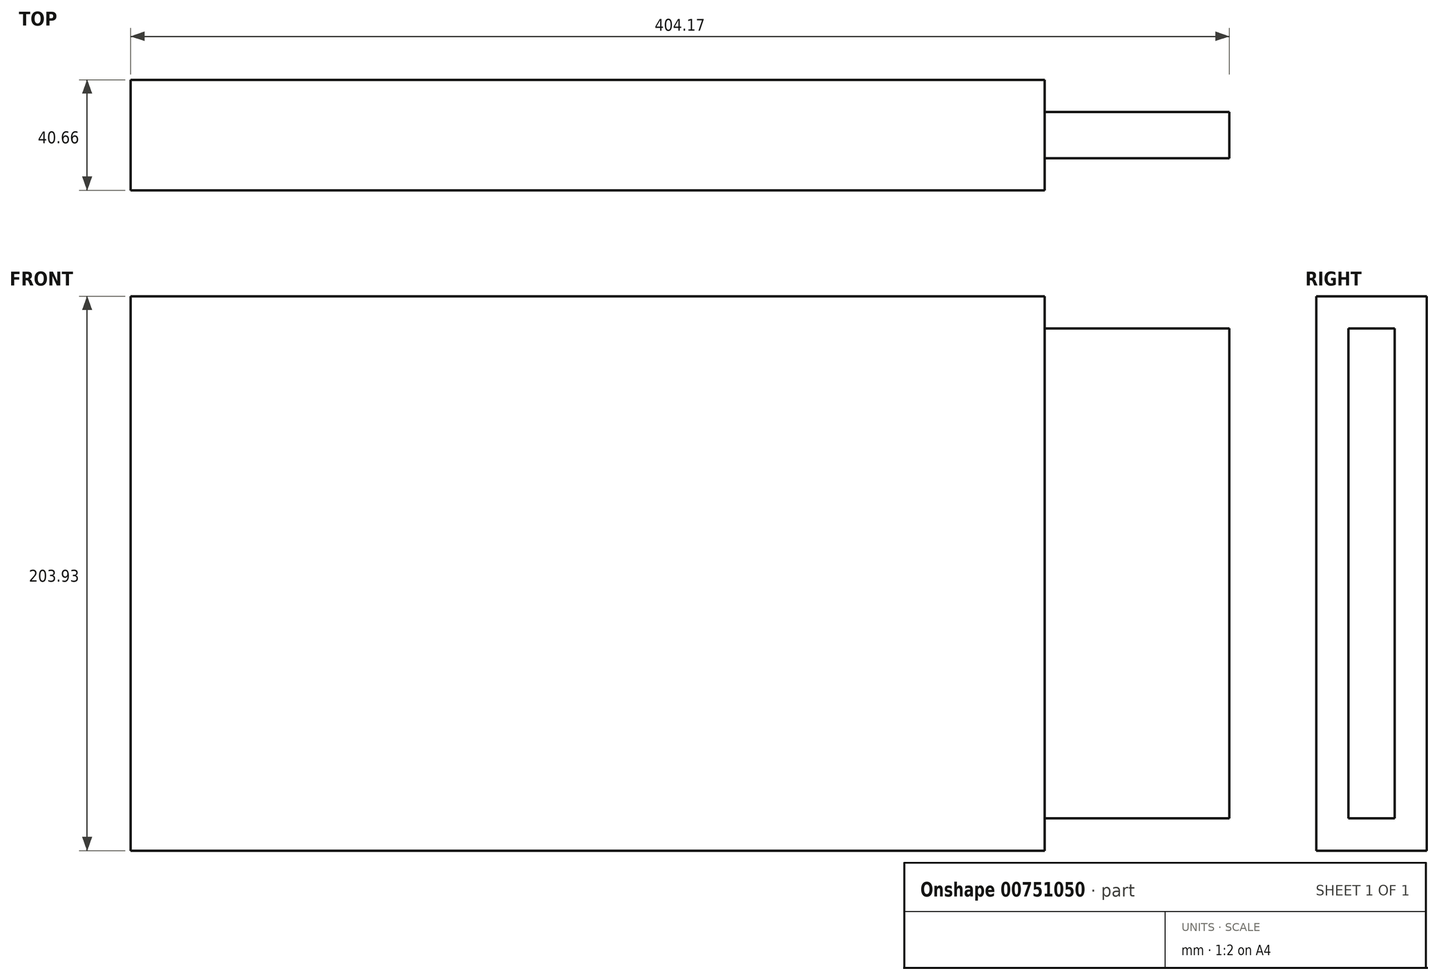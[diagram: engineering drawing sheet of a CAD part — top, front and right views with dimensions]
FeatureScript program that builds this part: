
annotation { "Feature Type Name" : "Feature", "Feature Type Description" : "" }
export const myFeature = defineFeature(function(context is Context, id is Id, definition is map)
    precondition{}
    {
        {
            var Q0;
            Q0=qCreatedBy(makeId("Right.planeOp"),FACE);
            var sketch = newSketch(context, id + "F0", { "sketchPlane" : qUnion([Q0])});
            skLineSegment(sketch, "E0.bottom", {"start": v(40.66, -91.28) * mm, "end": v(0, -91.28) * mm});
            skLineSegment(sketch, "E0.top", {"start": v(40.66, 112.65) * mm, "end": v(0, 112.65) * mm});
            skLineSegment(sketch, "E0.left", {"start": v(40.66, -91.28) * mm, "end": v(40.66, 112.65) * mm});
            skLineSegment(sketch, "E0.right", {"start": v(0, -91.28) * mm, "end": v(0, 112.65) * mm});
            skPoint(sketch, "E1.0", {"position": v(0, 0) * mm});
            skSolve(sketch);
        }
        {
            var Q0;
            Q0 = qSketchRegion(id + "F0", true);
            extrude(context, id + "F1", {"entities" : qUnion([Q0]), "depth" : 336.27 * mm, "offsetDistance" : 25.4 * mm});
        }
        {
            var Q0;
            Q0=makeQuery(id+"F1.opExtrude","CAP_FACE",FACE,{"disambiguationData":[OSD([sQuery(id+"F0.wireOp",EDGE,"E0.bottom"),sQuery(id+"F0.wireOp",EDGE,"E0.top"),sQuery(id+"F0.wireOp",EDGE,"E0.left"),sQuery(id+"F0.wireOp",EDGE,"E0.right")])],"isStart":false});
            var sketch = newSketch(context, id + "F2", { "sketchPlane" : qUnion([Q0])});
            skLineSegment(sketch, "E2.0", {"start": v(28.82, -79.44) * mm, "end": v(11.84, -79.44) * mm});
            skLineSegment(sketch, "E2.1", {"start": v(28.82, -79.44) * mm, "end": v(28.82, 100.8) * mm});
            skLineSegment(sketch, "E2.2", {"start": v(28.82, 100.8) * mm, "end": v(11.84, 100.8) * mm});
            skLineSegment(sketch, "E2.3", {"start": v(11.84, -79.44) * mm, "end": v(11.84, 100.8) * mm});
            skSolve(sketch);
        }
        {
            var Q0;
            Q0=makeQuery(id+"F2.imprint","IMPRINT",FACE,{"disambiguationData":[TD([[makeQuery(id+"F2.imprint","IMPRINT",EDGE,{"derivedFrom":sQuery(id+"F2.wireOp",EDGE,"E2.0")}),-1.0]])]});
            extrude(context, id + "F3", {"entities" : qUnion([Q0]), "operationType" : NewBodyOperationType.ADD, "depth" : 67.9 * mm, "offsetDistance" : 25.4 * mm});
        }
    });
